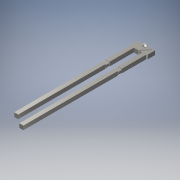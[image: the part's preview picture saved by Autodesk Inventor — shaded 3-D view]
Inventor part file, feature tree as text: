
AUTODESK INVENTOR PART (.ipt)
format: ipt  version: 2019.4 (Build 234330000, 330)  size: 336,384 bytes
history: native  units: mm
features: sketch x7, fillet x4, revolve x3, other x2, extrude x2, projected_geometry x2, sweep x1
ambient origin geometry x8: Origin, YZ Plane, XZ Plane, XY Plane, X Axis, Y Axis, Z Axis, Center Point
bodies: Body1 (feature_tree), Body2 (feature_tree)
feature tree (21):
  other  "Sólido1"
  extrude  "Extrusión1"  Depth=0.98mm
  extrude  "Extrusión2"  Depth=0.98mm
  fillet  "Empalme6"  Radius=4.0mm
  fillet  "Empalme7"  Radius=2.0mm
  fillet  "Empalme8"  Radius=1.0mm
  fillet  "Empalme9"  Radius=4.0mm
  revolve  "Revolución1"  [1 undecoded]
  revolve  "Revolución2"  [1 undecoded]
  revolve  "Revolución3"  [1 undecoded]
  sweep  "Barrido1"
  sketch  "Boceto1"  dims[d0=0.98mm d1=0.98mm]
  sketch  "Boceto2"  dims[d2=4.0mm d3=0.98mm d4=4.0mm d5=2.0mm d6=1.0mm d7=4.0mm]
  sketch  "Boceto3"  dims[d8=2.0mm d9=21.816616mm]
  sketch  "Boceto4"  dims[d10=9.599311mm d11=1.0mm]
  sketch  "Boceto5"  dims[d12=28.1mm d13=1.7mm]
  other  "Sólido2"
  sketch  "Boceto6"  dims[d14=0.98mm d15=0.0mm d16=1.18mm]
  projected_geometry  "Contorno proyectado1"
  projected_geometry  "Contorno proyectado2"
  sketch  "Boceto7"  dims[d17=1.18mm d20=0.1mm d21=0.1mm d22=0.78mm d23=0.0mm d29=0.1mm d30=0.1mm d31=0.1mm d32=0.1mm d33=180.0deg d34=180.0deg d35=180.0deg d36=0.1mm d37=0.0mm d38=0.0mm]
note: 3 required parameter values undecoded (feature->parameter linkage not recoverable at this tier; creation-order binding heuristic only, values carry confidence <= 0.55)
